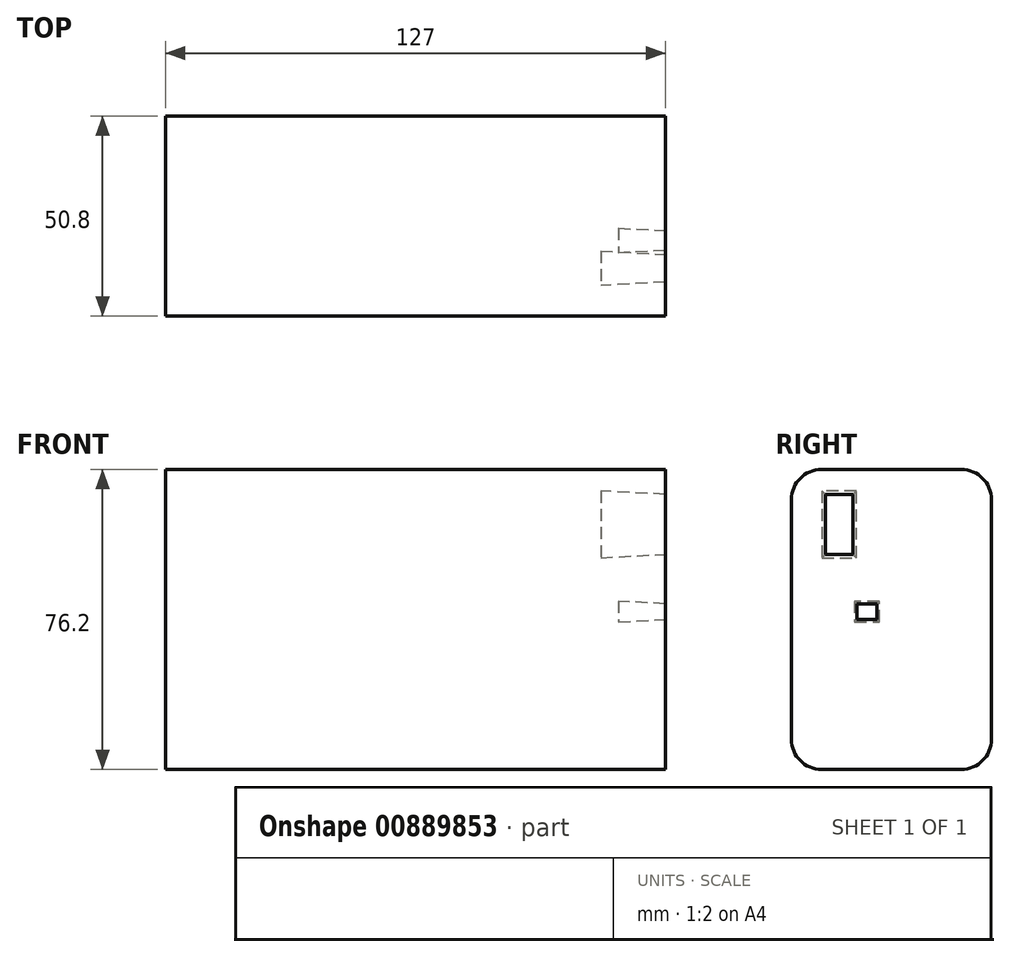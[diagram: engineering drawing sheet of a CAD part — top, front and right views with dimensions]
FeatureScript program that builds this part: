
annotation { "Feature Type Name" : "Feature", "Feature Type Description" : "" }
export const myFeature = defineFeature(function(context is Context, id is Id, definition is map)
    precondition{}
    {
        {
            var Q0;
            Q0=qCreatedBy(makeId("Front.planeOp"),FACE);
            var sketch = newSketch(context, id + "F0", { "sketchPlane" : qUnion([Q0])});
            skLineSegment(sketch, "E0.bottom", {"start": v(63.5, -38.1) * mm, "end": v(-63.5, -38.1) * mm});
            skLineSegment(sketch, "E0.top", {"start": v(63.5, 38.1) * mm, "end": v(-63.5, 38.1) * mm});
            skLineSegment(sketch, "E0.left", {"start": v(63.5, -38.1) * mm, "end": v(63.5, 38.1) * mm});
            skLineSegment(sketch, "E0.right", {"start": v(-63.5, -38.1) * mm, "end": v(-63.5, 38.1) * mm});
            skPoint(sketch, "E0.middle", {"position": v(0, 0) * mm});
            skSolve(sketch);
        }
        {
            var Q0;
            Q0=makeQuery(id+"F0.imprint","IMPRINT",FACE,{"disambiguationData":[TD([[makeQuery(id+"F0.imprint","IMPRINT",EDGE,{"derivedFrom":sQuery(id+"F0.wireOp",EDGE,"E0.bottom")}),-1.0]])]});
            extrude(context, id + "F1", {"entities" : qUnion([Q0]), "depth" : 50.8 * mm, "offsetDistance" : 25.4 * mm});
        }
        {
            var Q0;
            Q0=makeQuery(id+"F1.opExtrude","CAP_EDGE",EDGE,{"disambiguationData":[OSD([sQuery(id+"F0.wireOp",EDGE,"E0.top")])],"isStart":false});
            var Q1;
            Q1=makeQuery(id+"F1.opExtrude","CAP_EDGE",EDGE,{"disambiguationData":[OSD([sQuery(id+"F0.wireOp",EDGE,"E0.top")])],"isStart":true});
            var Q2;
            Q2=makeQuery(id+"F1.opExtrude","CAP_EDGE",EDGE,{"disambiguationData":[OSD([sQuery(id+"F0.wireOp",EDGE,"E0.bottom")])],"isStart":false});
            var Q3;
            Q3=makeQuery(id+"F1.opExtrude","CAP_EDGE",EDGE,{"disambiguationData":[OSD([sQuery(id+"F0.wireOp",EDGE,"E0.bottom")])],"isStart":true});
            fillet(context, id + "F2", {"entities" : qUnion([Q0, Q1, Q2, Q3]), "radius" : 7.62 * mm, "tangentPropagation" : true, "allowEdgeOverflow" : false});
        }
        {
            var Q0;
            Q0=makeQuery(id+"F1.opExtrude","SWEPT_FACE",FACE,{"disambiguationData":[OSD([sQuery(id+"F0.wireOp",EDGE,"E0.left")])]});
            var sketch = newSketch(context, id + "F3", { "sketchPlane" : qUnion([Q0])});
            skLineSegment(sketch, "E1.bottom", {"start": v(-42.16, 31.8) * mm, "end": v(-35.16, 31.8) * mm});
            skLineSegment(sketch, "E1.top", {"start": v(-42.16, 16.55) * mm, "end": v(-35.16, 16.55) * mm});
            skLineSegment(sketch, "E1.left", {"start": v(-42.16, 31.8) * mm, "end": v(-42.16, 16.55) * mm});
            skLineSegment(sketch, "E1.right", {"start": v(-35.16, 31.8) * mm, "end": v(-35.16, 16.55) * mm});
            skSolve(sketch);
        }
        {
            var Q0;
            Q0=makeQuery(id+"F3.imprint","IMPRINT",FACE,{"disambiguationData":[TD([[makeQuery(id+"F3.imprint","IMPRINT",EDGE,{"derivedFrom":sQuery(id+"F3.wireOp",EDGE,"E1.bottom")}),-1.0]])]});
            extrude(context, id + "F4", {"entities" : qUnion([Q0]), "operationType" : NewBodyOperationType.REMOVE, "oppositeDirection" : true, "depth" : 16.4 * mm, "offsetDistance" : 25.4 * mm, "hasDraft" : true, "draftAngle" : 3 * degree});
        }
        {
            var Q0;
            Q0=makeQuery(id+"F1.opExtrude","SWEPT_FACE",FACE,{"disambiguationData":[OSD([sQuery(id+"F0.wireOp",EDGE,"E0.left")])]});
            var sketch = newSketch(context, id + "F5", { "sketchPlane" : qUnion([Q0])});
            skLineSegment(sketch, "E2.bottom", {"start": v(-34.12, 4) * mm, "end": v(-29.12, 4) * mm});
            skLineSegment(sketch, "E2.top", {"start": v(-34.12, 0) * mm, "end": v(-29.12, 0) * mm});
            skLineSegment(sketch, "E2.left", {"start": v(-34.12, 4) * mm, "end": v(-34.12, 0) * mm});
            skLineSegment(sketch, "E2.right", {"start": v(-29.12, 4) * mm, "end": v(-29.12, 0) * mm});
            skSolve(sketch);
        }
        {
            var Q0;
            Q0 = qSketchRegion(id + "F5", true);
            extrude(context, id + "F6", {"entities" : qUnion([Q0]), "operationType" : NewBodyOperationType.REMOVE, "oppositeDirection" : true, "depth" : 11.94 * mm, "offsetDistance" : 25.4 * mm, "hasDraft" : true, "draftAngle" : 3 * degree});
        }
    });
